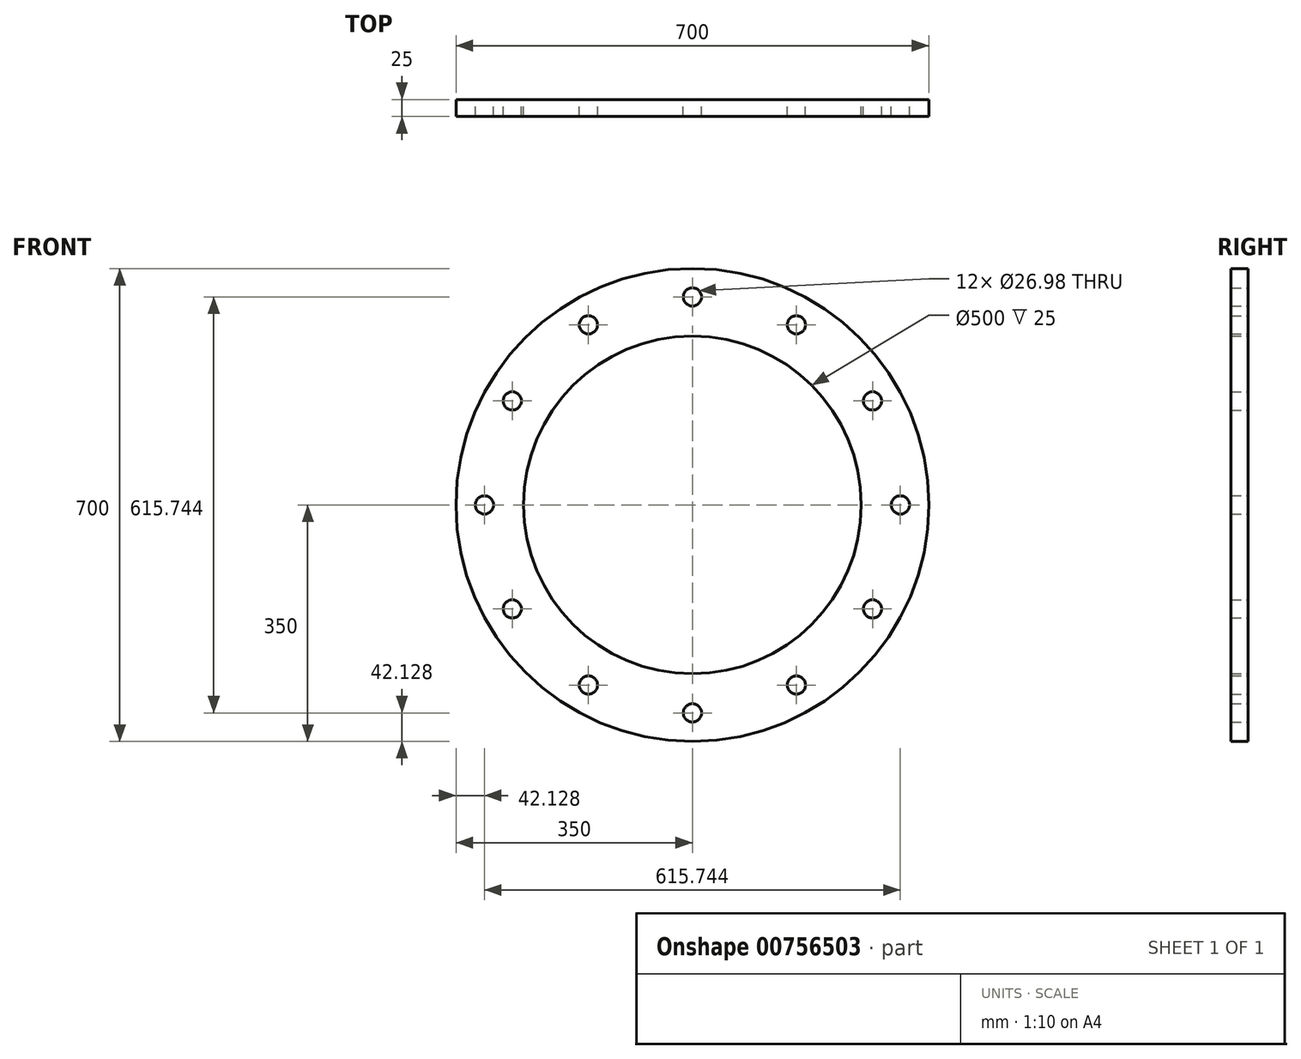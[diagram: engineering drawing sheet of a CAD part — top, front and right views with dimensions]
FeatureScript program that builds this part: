
annotation { "Feature Type Name" : "Feature", "Feature Type Description" : "" }
export const myFeature = defineFeature(function(context is Context, id is Id, definition is map)
    precondition{}
    {
        {
            var Q0;
            Q0=qCreatedBy(makeId("Front.planeOp"),FACE);
            var sketch = newSketch(context, id + "F0", { "sketchPlane" : qUnion([Q0])});
            skCircle(sketch, "E0", {"center": v(0, 0) * mm, "radius": 250 * mm});
            skCircle(sketch, "E1", {"center": v(0, 0) * mm, "radius": 350 * mm});
            skCircle(sketch, "E2", {"center": v(0, 307.87) * mm, "radius": 13.5 * mm});
            skCircle(sketch, "E3.1.0", {"center": v(153.94, 266.63) * mm, "radius": 13.5 * mm});
            skCircle(sketch, "E3.2.0", {"center": v(266.63, 153.94) * mm, "radius": 13.5 * mm});
            skCircle(sketch, "E3.3.0", {"center": v(307.87, 0) * mm, "radius": 13.5 * mm});
            skCircle(sketch, "E3.4.0", {"center": v(266.63, -153.94) * mm, "radius": 13.5 * mm});
            skCircle(sketch, "E3.5.0", {"center": v(153.94, -266.63) * mm, "radius": 13.5 * mm});
            skCircle(sketch, "E3.6.0", {"center": v(0, -307.87) * mm, "radius": 13.5 * mm});
            skCircle(sketch, "E3.7.0", {"center": v(-153.94, -266.63) * mm, "radius": 13.5 * mm});
            skCircle(sketch, "E3.8.0", {"center": v(-266.63, -153.94) * mm, "radius": 13.5 * mm});
            skCircle(sketch, "E3.9.0", {"center": v(-307.87, 0) * mm, "radius": 13.5 * mm});
            skCircle(sketch, "E3.10.0", {"center": v(-266.63, 153.94) * mm, "radius": 13.5 * mm});
            skCircle(sketch, "E3.11.0", {"center": v(-153.94, 266.63) * mm, "radius": 13.5 * mm});
            skLineSegment(sketch, "E3.anchor1", {"start": v(0, 0) * mm, "end": v(0, 307.87) * mm, "construction": true});
            skLineSegment(sketch, "E3.anchor2", {"start": v(0, 0) * mm, "end": v(-153.94, 266.63) * mm, "construction": true});
            skSolve(sketch);
        }
        {
            var Q0;
            Q0=makeQuery(id+"F0.imprint","IMPRINT",FACE,{"disambiguationData":[TD([[makeQuery(id+"F0.imprint","IMPRINT",EDGE,{"derivedFrom":sQuery(id+"F0.wireOp",EDGE,"E0")}),-1.0]])]});
            extrude(context, id + "F1", {"entities" : qUnion([Q0]), "depth" : 25 * mm, "offsetDistance" : 25 * mm});
        }
    });
